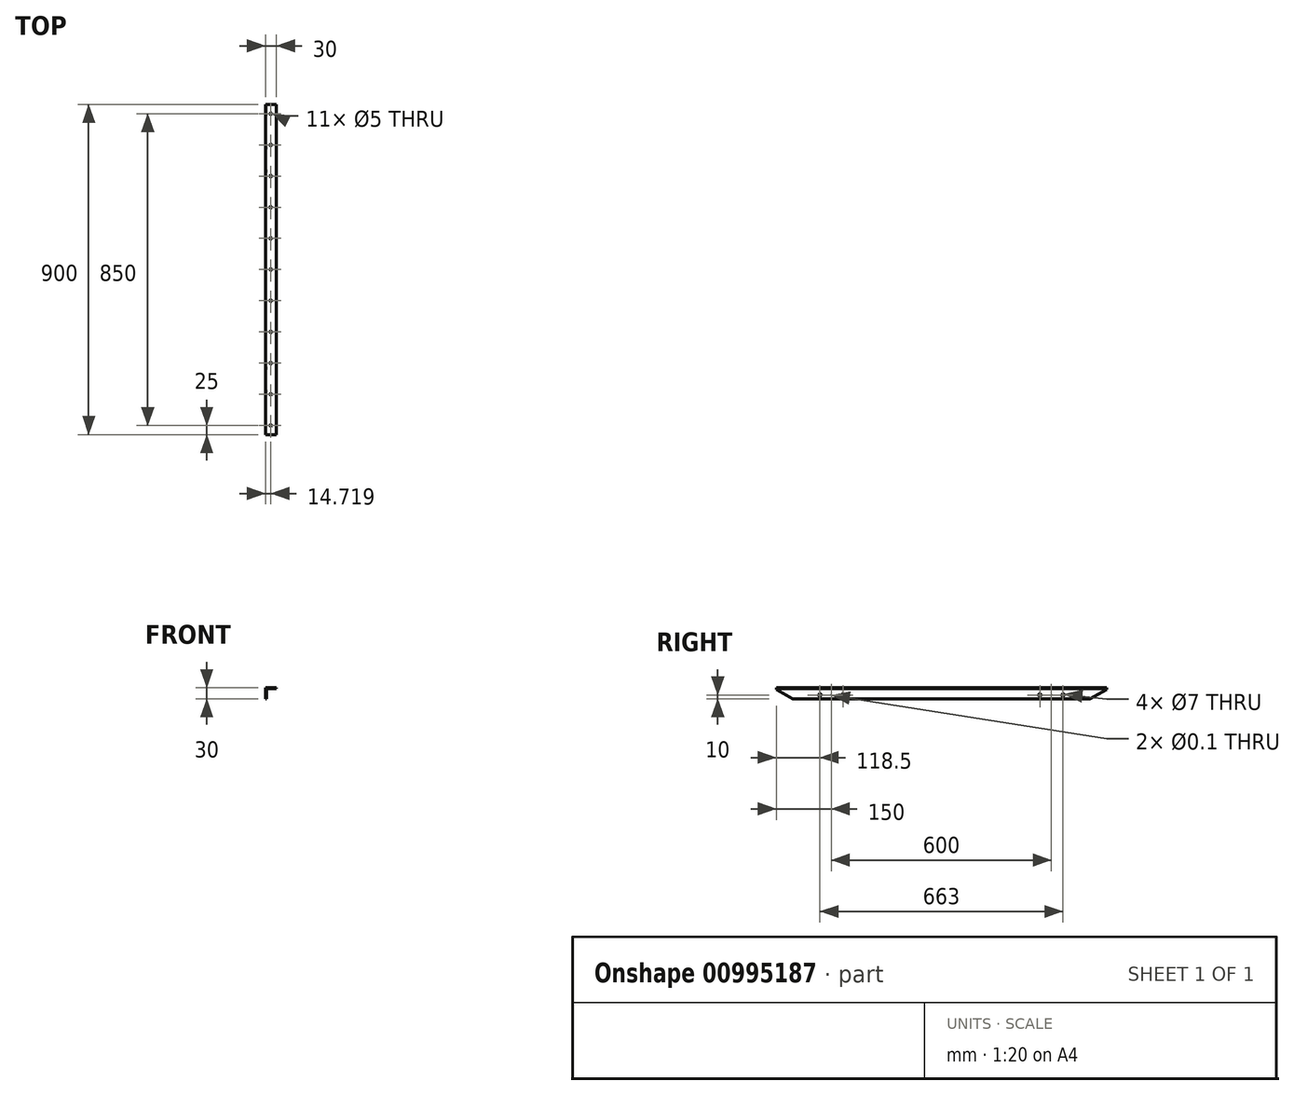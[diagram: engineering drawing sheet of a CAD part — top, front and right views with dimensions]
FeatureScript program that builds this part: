
annotation { "Feature Type Name" : "Feature", "Feature Type Description" : "" }
export const myFeature = defineFeature(function(context is Context, id is Id, definition is map)
    precondition{}
    {
        {
            var Q0;
            Q0=qCreatedBy(makeId("Front.planeOp"),FACE);
            var sketch = newSketch(context, id + "F0", { "sketchPlane" : qUnion([Q0])});
            skLineSegment(sketch, "E0", {"start": v(0, 0) * mm, "end": v(0, 30) * mm});
            skLineSegment(sketch, "E1", {"start": v(0, 30) * mm, "end": v(30, 30) * mm});
            skLineSegment(sketch, "E2", {"start": v(30, 30) * mm, "end": v(30, 27) * mm});
            skLineSegment(sketch, "E3", {"start": v(30, 27) * mm, "end": v(3, 27) * mm});
            skLineSegment(sketch, "E4", {"start": v(3, 27) * mm, "end": v(3, 0) * mm});
            skLineSegment(sketch, "E5", {"start": v(3, 0) * mm, "end": v(0, 0) * mm});
            skSolve(sketch);
        }
        {
            var Q0;
            Q0=makeQuery(id+"F0.imprint","IMPRINT",FACE,{"disambiguationData":[TD([[makeQuery(id+"F0.imprint","IMPRINT",EDGE,{"derivedFrom":sQuery(id+"F0.wireOp",EDGE,"E0")}),-1.0]])]});
            extrude(context, id + "F1", {"entities" : qUnion([Q0]), "depth" : 900 * mm, "offsetDistance" : 25 * mm, "symmetric" : true});
        }
        {
            var Q0;
            Q0=makeQuery(id+"F1.opExtrude","SWEPT_FACE",FACE,{"disambiguationData":[OSD([sQuery(id+"F0.wireOp",EDGE,"E0")])]});
            var sketch = newSketch(context, id + "F2", { "sketchPlane" : qUnion([Q0])});
            skLineSegment(sketch, "E6", {"start": v(0, 30) * mm, "end": v(0, 10) * mm});
            skLineSegment(sketch, "E7", {"start": v(0, 10) * mm, "end": v(-300, 10) * mm});
            skLineSegment(sketch, "E8", {"start": v(0, 10) * mm, "end": v(300, 10) * mm});
            skLineSegment(sketch, "E9", {"start": v(300, 10) * mm, "end": v(331.5, 10) * mm});
            skLineSegment(sketch, "E10", {"start": v(-300, 10) * mm, "end": v(-331.5, 10) * mm});
            skLineSegment(sketch, "E11", {"start": v(-300, 10) * mm, "end": v(-268.5, 10) * mm});
            skLineSegment(sketch, "E12", {"start": v(300, 10) * mm, "end": v(268.5, 10) * mm});
            skSolve(sketch);
        }
        {
            var Q0;
            Q0=sQuery(id+"F2.wireOp",VERTEX,"E7.end");
            var Q1;
            Q1=sQuery(id+"F2.wireOp",VERTEX,"E8.end");
            var Q2;
            Q2=makeQuery(id+"F1.opExtrude","SWEPT_BODY",BODY,{"disambiguationData":[OSD([sQuery(id+"F0.wireOp",EDGE,"E0"),sQuery(id+"F0.wireOp",EDGE,"E1"),sQuery(id+"F0.wireOp",EDGE,"E2"),sQuery(id+"F0.wireOp",EDGE,"E3"),sQuery(id+"F0.wireOp",EDGE,"E4"),sQuery(id+"F0.wireOp",EDGE,"E5")])]});
            hole(context, id + "F3", {"style" : HoleStyle.SIMPLE, "endStyle" : HoleEndStyle.THROUGH, "holeDiameter" : 0.1 * mm, "majorDiameter" : 5 * mm, "isTappedThrough" : true, "tappedDepth" : 12 * mm, "tapClearance" : 3, "locations" : qUnion([Q0, Q1]), "scope" : qUnion([Q2]), "startStyle" : HoleStartStyle.PART});
        }
        {
            var Q0;
            Q0=makeQuery(id+"F1.opExtrude","SWEPT_FACE",FACE,{"disambiguationData":[OSD([sQuery(id+"F0.wireOp",EDGE,"E1")])]});
            var sketch = newSketch(context, id + "F4", { "sketchPlane" : qUnion([Q0])});
            skLineSegment(sketch, "E13", {"start": v(0, 0) * mm, "end": v(14.72, 0) * mm});
            skLineSegment(sketch, "E14", {"start": v(14.72, 0) * mm, "end": v(14.72, 85) * mm});
            skLineSegment(sketch, "E15", {"start": v(14.72, 85) * mm, "end": v(14.72, 170) * mm});
            skLineSegment(sketch, "E16", {"start": v(14.72, 170) * mm, "end": v(14.72, 255) * mm});
            skLineSegment(sketch, "E17", {"start": v(14.72, 0) * mm, "end": v(14.72, -85) * mm});
            skLineSegment(sketch, "E18", {"start": v(14.72, -85) * mm, "end": v(14.72, -170) * mm});
            skLineSegment(sketch, "E19", {"start": v(14.72, -170) * mm, "end": v(14.72, -255) * mm});
            skLineSegment(sketch, "E20", {"start": v(14.72, -255) * mm, "end": v(14.72, -340) * mm});
            skLineSegment(sketch, "E21", {"start": v(14.72, -340) * mm, "end": v(14.72, -425) * mm});
            skLineSegment(sketch, "E22", {"start": v(14.72, 255) * mm, "end": v(14.72, 340) * mm});
            skLineSegment(sketch, "E23", {"start": v(14.72, 340) * mm, "end": v(14.72, 425) * mm});
            skSolve(sketch);
        }
        {
            var Q0;
            Q0=sQuery(id+"F4.wireOp",VERTEX,"E16.end");
            var Q1;
            Q1=sQuery(id+"F4.wireOp",VERTEX,"E16.start");
            var Q2;
            Q2=sQuery(id+"F4.wireOp",VERTEX,"E15.start");
            var Q3;
            Q3=sQuery(id+"F4.wireOp",VERTEX,"E17.start");
            var Q4;
            Q4=sQuery(id+"F4.wireOp",VERTEX,"E18.start");
            var Q5;
            Q5=sQuery(id+"F4.wireOp",VERTEX,"E19.start");
            var Q6;
            Q6=sQuery(id+"F4.wireOp",VERTEX,"E19.end");
            var Q7;
            Q7=sQuery(id+"F4.wireOp",VERTEX,"gbc2nK7E-ztz0-IBhr-DfQU-EQeF7ijxsCjM.end");
            var Q8;
            Q8=sQuery(id+"F4.wireOp",VERTEX,"ZtBBAAtL-lso0-mhiq-NLzV-Yrly4486QW8c.end");
            var Q9;
            Q9=sQuery(id+"F4.wireOp",VERTEX,"E22.end");
            var Q10;
            Q10=sQuery(id+"F4.wireOp",VERTEX,"E23.end");
            var Q11;
            Q11=sQuery(id+"F4.wireOp",VERTEX,"E20.end");
            var Q12;
            Q12=sQuery(id+"F4.wireOp",VERTEX,"E21.end");
            var Q13;
            Q13=makeQuery(id+"F1.opExtrude","SWEPT_BODY",BODY,{"disambiguationData":[OSD([sQuery(id+"F0.wireOp",EDGE,"E0"),sQuery(id+"F0.wireOp",EDGE,"E1"),sQuery(id+"F0.wireOp",EDGE,"E2"),sQuery(id+"F0.wireOp",EDGE,"E3"),sQuery(id+"F0.wireOp",EDGE,"E4"),sQuery(id+"F0.wireOp",EDGE,"E5")])]});
            hole(context, id + "F5", {"style" : HoleStyle.SIMPLE, "endStyle" : HoleEndStyle.THROUGH, "holeDiameter" : 5 * mm, "majorDiameter" : 5 * mm, "isTappedThrough" : true, "tappedDepth" : 12 * mm, "tapClearance" : 3, "locations" : qUnion([Q0, Q1, Q2, Q3, Q4, Q5, Q6, Q7, Q8, Q9, Q10, Q11, Q12]), "scope" : qUnion([Q13]), "startStyle" : HoleStartStyle.PART});
        }
        {
            var Q0;
            Q0=makeQuery(id+"F1.opExtrude","SWEPT_FACE",FACE,{"disambiguationData":[OSD([sQuery(id+"F0.wireOp",EDGE,"E0")])]});
            var sketch = newSketch(context, id + "F6", { "sketchPlane" : qUnion([Q0])});
            skLineSegment(sketch, "E24", {"start": v(-450, 25) * mm, "end": v(-450, 0) * mm});
            skLineSegment(sketch, "E25", {"start": v(-450, 0) * mm, "end": v(-405, 0) * mm});
            skLineSegment(sketch, "E26", {"start": v(-405, 0) * mm, "end": v(-450, 25) * mm});
            skLineSegment(sketch, "E27", {"start": v(450, 25) * mm, "end": v(450, 0) * mm});
            skLineSegment(sketch, "E28", {"start": v(450, 0) * mm, "end": v(405, 0) * mm});
            skLineSegment(sketch, "E29", {"start": v(405, 0) * mm, "end": v(450, 25) * mm});
            skSolve(sketch);
        }
        {
            var Q0;
            Q0=qSketchRegion(id+"F6",true);
            extrude(context, id + "F7", {"entities" : qUnion([Q0]), "operationType" : NewBodyOperationType.REMOVE, "oppositeDirection" : true, "depth" : 25 * mm, "offsetDistance" : 25 * mm});
        }
        {
            var Q0;
            Q0=sQuery(id+"F2.wireOp",VERTEX,"E9.end");
            var Q1;
            Q1=sQuery(id+"F2.wireOp",VERTEX,"E12.end");
            var Q2;
            Q2=sQuery(id+"F2.wireOp",VERTEX,"E10.end");
            var Q3;
            Q3=sQuery(id+"F2.wireOp",VERTEX,"E11.end");
            var Q4;
            Q4=makeQuery(id+"F1.opExtrude","SWEPT_BODY",BODY,{"disambiguationData":[OSD([sQuery(id+"F0.wireOp",EDGE,"E0"),sQuery(id+"F0.wireOp",EDGE,"E1"),sQuery(id+"F0.wireOp",EDGE,"E2"),sQuery(id+"F0.wireOp",EDGE,"E3"),sQuery(id+"F0.wireOp",EDGE,"E4"),sQuery(id+"F0.wireOp",EDGE,"E5")])]});
            hole(context, id + "F8", {"style" : HoleStyle.SIMPLE, "endStyle" : HoleEndStyle.THROUGH, "holeDiameter" : 7 * mm, "majorDiameter" : 5 * mm, "isTappedThrough" : true, "tappedDepth" : 12 * mm, "tapClearance" : 3, "locations" : qUnion([Q0, Q1, Q2, Q3]), "scope" : qUnion([Q4]), "startStyle" : HoleStartStyle.PART});
        }
    });
